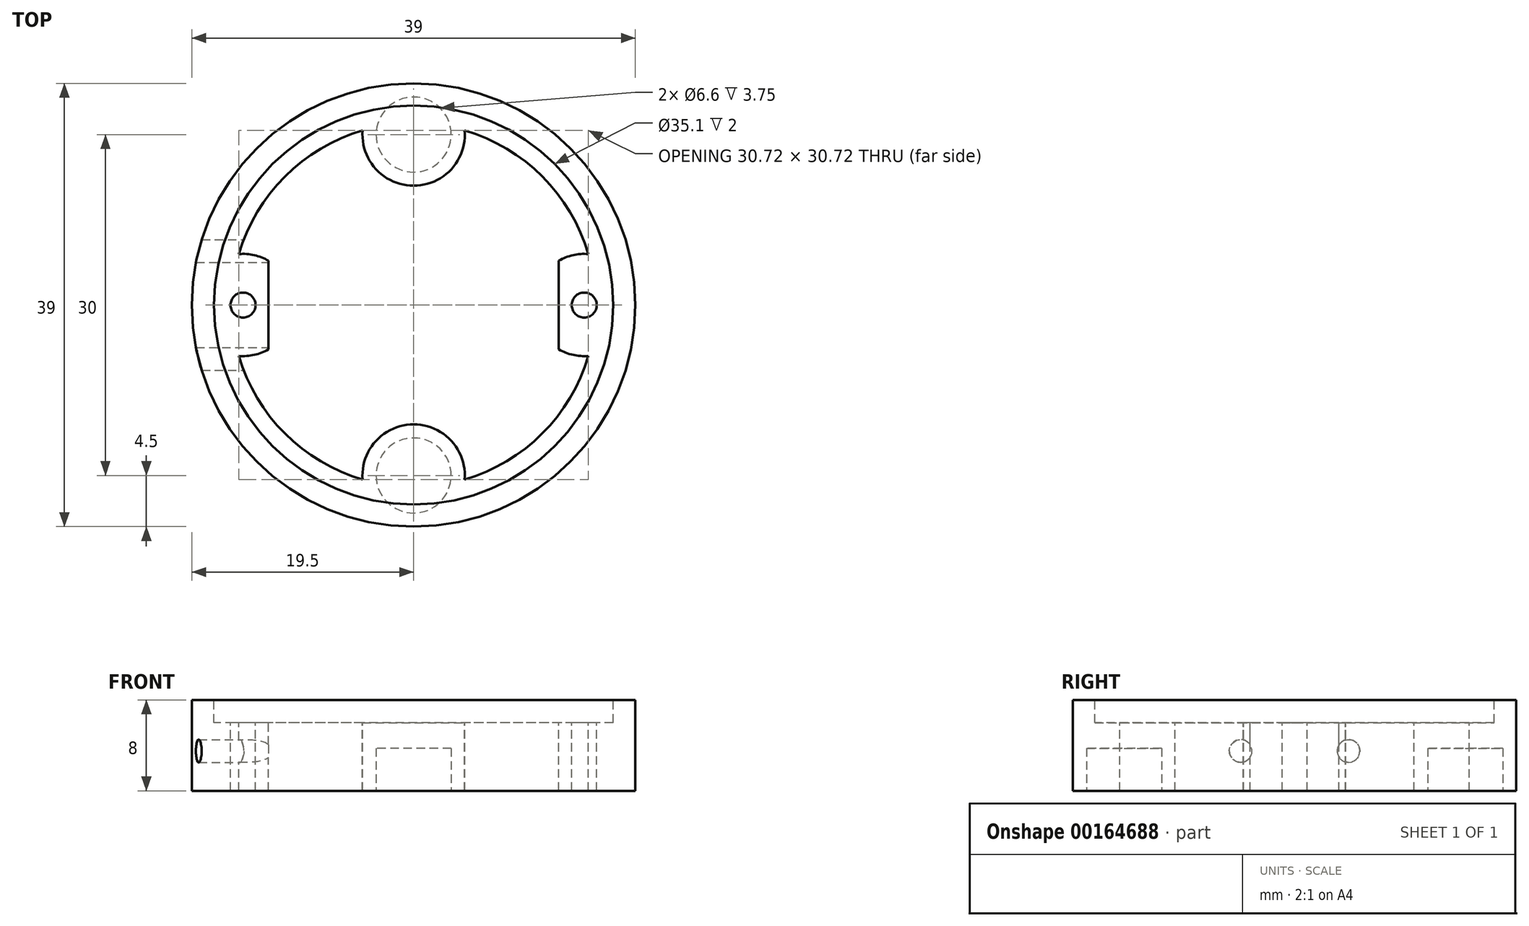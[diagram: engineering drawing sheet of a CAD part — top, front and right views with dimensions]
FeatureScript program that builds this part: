
annotation { "Feature Type Name" : "Feature", "Feature Type Description" : "" }
export const myFeature = defineFeature(function(context is Context, id is Id, definition is map)
    precondition{}
    {
        {
            var Q0;
            Q0=qCreatedBy(makeId("Top.planeOp"),FACE);
            var sketch = newSketch(context, id + "F0", { "sketchPlane" : qUnion([Q0])});
            skCircle(sketch, "E0", {"center": v(0, 0) * mm, "radius": 19.5 * mm});
            skSolve(sketch);
        }
        {
            var Q0;
            Q0 = qSketchRegion(id + "F0", true);
            extrude(context, id + "F1", {"entities" : qUnion([Q0]), "depth" : 8 * mm});
        }
        {
            var Q0;
            Q0=makeQuery(id+"F1.opExtrude","CAP_FACE",FACE,{"disambiguationData":[OSD([sQuery(id+"F0.wireOp",EDGE,"E0")])],"isStart":false});
            var sketch = newSketch(context, id + "F2", { "sketchPlane" : qUnion([Q0])});
            skCircle(sketch, "E1", {"center": v(0, 0) * mm, "radius": 17.55 * mm});
            skSolve(sketch);
        }
        {
            var Q0;
            Q0 = qSketchRegion(id + "F2", true);
            extrude(context, id + "F3", {"entities" : qUnion([Q0]), "operationType" : NewBodyOperationType.REMOVE, "oppositeDirection" : true, "depth" : 2 * mm});
        }
        {
            var Q0;
            Q0=makeQuery(id+"F3.boolean.opBoolean","COPY",FACE,{"derivedFrom":makeQuery(id+"F3.opExtrude","CAP_FACE",FACE,{"disambiguationData":[OSD([sQuery(id+"F2.wireOp",EDGE,"E1")])],"isStart":false})});
            var sketch = newSketch(context, id + "F4", { "sketchPlane" : qUnion([Q0])});
            skArc(sketch, "E2", {"start": v(15.36, 4.49) * mm, "mid": v(10.5, 0) * mm, "end": v(15.36, -4.49) * mm});
            skLineSegment(sketch, "E3", {"start": v(0, 0) * mm, "end": v(22.83, 22.83) * mm, "construction": true});
            skArc(sketch, "E4.MirrorC", {"start": v(4.49, 15.36) * mm, "mid": v(0, 10.5) * mm, "end": v(-4.49, 15.36) * mm});
            skArc(sketch, "E5.MirrorC", {"start": v(4.49, -15.36) * mm, "mid": v(0, -10.5) * mm, "end": v(-4.49, -15.36) * mm});
            skArc(sketch, "E6.MirrorC", {"start": v(-15.36, 4.49) * mm, "mid": v(-10.5, 0) * mm, "end": v(-15.36, -4.49) * mm});
            skArc(sketch, "E7", {"start": v(-4.49, 15.36) * mm, "mid": v(-11.31, 11.31) * mm, "end": v(-15.36, 4.49) * mm});
            skArc(sketch, "E8.trimOffspring", {"start": v(15.36, 4.49) * mm, "mid": v(11.31, 11.31) * mm, "end": v(4.49, 15.36) * mm});
            skArc(sketch, "E9.trimOffspring", {"start": v(-15.36, -4.49) * mm, "mid": v(-11.31, -11.31) * mm, "end": v(-4.49, -15.36) * mm});
            skArc(sketch, "E10.trimOffspring", {"start": v(4.49, -15.36) * mm, "mid": v(11.31, -11.31) * mm, "end": v(15.36, -4.49) * mm});
            skSolve(sketch);
        }
        {
            var Q0;
            Q0 = qSketchRegion(id + "F4", true);
            extrude(context, id + "F5", {"entities" : qUnion([Q0]), "operationType" : NewBodyOperationType.REMOVE, "oppositeDirection" : true, "depth" : 6 * mm});
        }
        {
            var Q0;
            Q0=makeQuery(id+"F3.boolean.opBoolean","COPY",FACE,{"derivedFrom":makeQuery(id+"F3.opExtrude","CAP_FACE",FACE,{"disambiguationData":[OSD([sQuery(id+"F2.wireOp",EDGE,"E1")])],"isStart":false})});
            var sketch = newSketch(context, id + "F6", { "sketchPlane" : qUnion([Q0])});
            skCircle(sketch, "E11", {"center": v(-15, 0) * mm, "radius": 1.1 * mm});
            skCircle(sketch, "E12.MirrorC", {"center": v(15, 0) * mm, "radius": 1.1 * mm});
            skSolve(sketch);
        }
        {
            var Q0;
            Q0 = qSketchRegion(id + "F6", true);
            extrude(context, id + "F7", {"entities" : qUnion([Q0]), "operationType" : NewBodyOperationType.REMOVE, "oppositeDirection" : true, "depth" : 6 * mm});
        }
        {
            var Q0;
            Q0=qCreatedBy(makeId("Top.planeOp"),FACE);
            var sketch = newSketch(context, id + "F8", { "sketchPlane" : qUnion([Q0])});
            skCircle(sketch, "E13", {"center": v(0, 15) * mm, "radius": 3.3 * mm});
            skCircle(sketch, "E14.MirrorC", {"center": v(0, -15) * mm, "radius": 3.3 * mm});
            skSolve(sketch);
        }
        {
            var Q0;
            Q0 = qSketchRegion(id + "F8", true);
            extrude(context, id + "F9", {"entities" : qUnion([Q0]), "operationType" : NewBodyOperationType.REMOVE, "depth" : 3.75 * mm});
        }
        {
            var Q0;
            Q0=qCreatedBy(makeId("Right.planeOp"),FACE);
            var sketch = newSketch(context, id + "F10", { "sketchPlane" : qUnion([Q0])});
            skCircle(sketch, "E15", {"center": v(-4.74, 3.5) * mm, "radius": 1 * mm});
            skCircle(sketch, "E16.MirrorC", {"center": v(4.74, 3.5) * mm, "radius": 1 * mm});
            skSolve(sketch);
        }
        {
            var Q0;
            Q0 = qSketchRegion(id + "F10", true);
            extrude(context, id + "F11", {"entities" : qUnion([Q0]), "operationType" : NewBodyOperationType.REMOVE, "oppositeDirection" : true, "depth" : 25 * mm});
        }
        {
            var Q0;
            Q0=makeQuery(id+"F3.boolean.opBoolean","COPY",FACE,{"derivedFrom":makeQuery(id+"F3.opExtrude","CAP_FACE",FACE,{"disambiguationData":[OSD([sQuery(id+"F2.wireOp",EDGE,"E1")])],"isStart":false})});
            var sketch = newSketch(context, id + "F12", { "sketchPlane" : qUnion([Q0])});
            skLineSegment(sketch, "E17.bottom", {"start": v(-12.77, 5.24) * mm, "end": v(-9.52, 5.24) * mm});
            skLineSegment(sketch, "E17.top", {"start": v(-12.77, -5.46) * mm, "end": v(-9.52, -5.46) * mm});
            skLineSegment(sketch, "E17.left", {"start": v(-12.77, 5.24) * mm, "end": v(-12.77, -5.46) * mm});
            skLineSegment(sketch, "E17.right", {"start": v(-9.52, 5.24) * mm, "end": v(-9.52, -5.46) * mm});
            skLineSegment(sketch, "E18.MirrorCS", {"start": v(12.77, 5.24) * mm, "end": v(9.52, 5.24) * mm});
            skLineSegment(sketch, "E19.MirrorCS", {"start": v(12.77, 5.24) * mm, "end": v(12.77, -5.46) * mm});
            skLineSegment(sketch, "E20.MirrorCS", {"start": v(9.52, 5.24) * mm, "end": v(9.52, -5.46) * mm});
            skLineSegment(sketch, "E21.MirrorCS", {"start": v(12.77, -5.46) * mm, "end": v(9.52, -5.46) * mm});
            skSolve(sketch);
        }
        {
            var Q0;
            Q0 = qSketchRegion(id + "F12", true);
            extrude(context, id + "F13", {"entities" : qUnion([Q0]), "operationType" : NewBodyOperationType.REMOVE, "oppositeDirection" : true, "depth" : 6 * mm});
        }
    });
